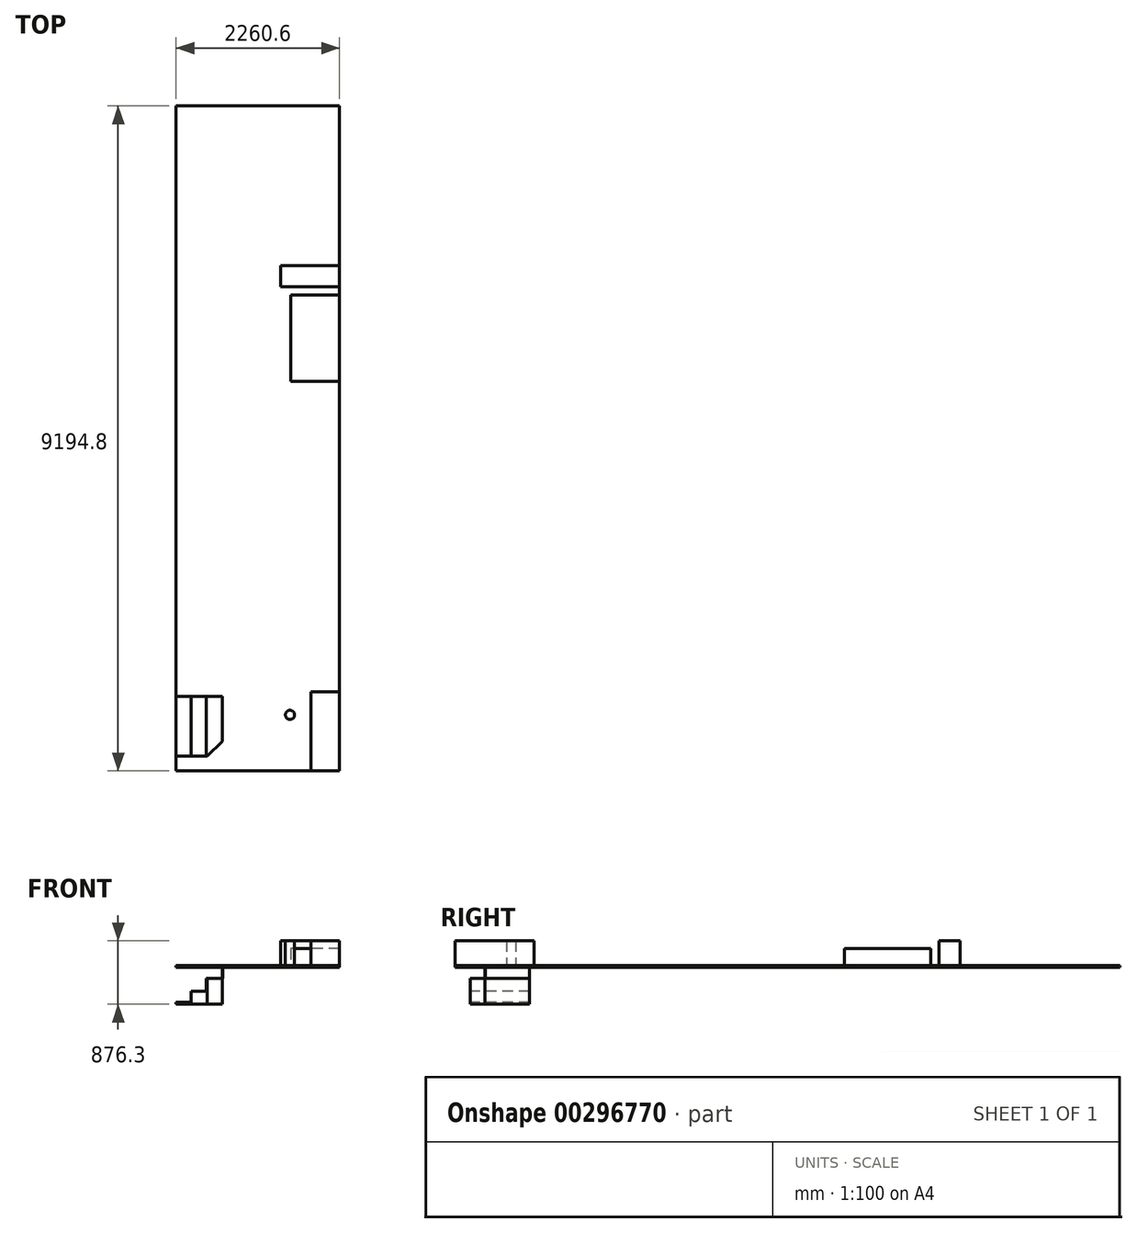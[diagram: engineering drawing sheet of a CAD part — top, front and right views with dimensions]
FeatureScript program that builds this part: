
annotation { "Feature Type Name" : "Feature", "Feature Type Description" : "" }
export const myFeature = defineFeature(function(context is Context, id is Id, definition is map)
    precondition{}
    {
        {
            var Q0;
            Q0=qCreatedBy(makeId("Top.planeOp"),FACE);
            var sketch = newSketch(context, id + "F0", { "sketchPlane" : qUnion([Q0])});
            skLineSegment(sketch, "E0.bottom", {"start": v(0, 0) * mm, "end": v(1016, 0) * mm});
            skLineSegment(sketch, "E0.top", {"start": v(0, 1930.4) * mm, "end": v(1016, 1930.4) * mm});
            skLineSegment(sketch, "E0.left", {"start": v(0, 0) * mm, "end": v(0, 1930.4) * mm});
            skLineSegment(sketch, "E0.right", {"start": v(1016, 0) * mm, "end": v(1016, 1930.4) * mm});
            skLineSegment(sketch, "E1.bottom", {"start": v(1016, 1930.4) * mm, "end": v(-203.2, 1930.4) * mm});
            skLineSegment(sketch, "E1.top", {"start": v(1016, 4064) * mm, "end": v(-203.2, 4064) * mm});
            skLineSegment(sketch, "E1.left", {"start": v(1016, 1930.4) * mm, "end": v(1016, 4064) * mm});
            skLineSegment(sketch, "E1.right", {"start": v(-203.2, 1930.4) * mm, "end": v(-203.2, 4064) * mm});
            skLineSegment(sketch, "E2.bottom", {"start": v(-1244.6, 635) * mm, "end": v(-635, 635) * mm});
            skLineSegment(sketch, "E2.left", {"start": v(-1244.6, 635) * mm, "end": v(-1244.6, 1244.6) * mm});
            skLineSegment(sketch, "E2.right", {"start": v(-635, 635) * mm, "end": v(-635, 1270) * mm});
            skLineSegment(sketch, "E3", {"start": v(-1244.6, 1244.6) * mm, "end": v(-1244.6, 1651) * mm});
            skLineSegment(sketch, "E4", {"start": v(-1244.6, 1651) * mm, "end": v(-635, 1270) * mm});
            skLineSegment(sketch, "E5.bottom", {"start": v(1016, 0) * mm, "end": v(-1244.6, 0) * mm});
            skLineSegment(sketch, "E5.top", {"start": v(1016, 4165.6) * mm, "end": v(-1244.6, 4165.6) * mm});
            skLineSegment(sketch, "E5.left", {"start": v(1016, 0) * mm, "end": v(1016, 4165.6) * mm});
            skLineSegment(sketch, "E5.right", {"start": v(-1244.6, 0) * mm, "end": v(-1244.6, 4165.6) * mm});
            skLineSegment(sketch, "E6.top", {"start": v(1016, 5359.4) * mm, "end": v(-1244.6, 5359.4) * mm});
            skLineSegment(sketch, "E6.left", {"start": v(1016, 4165.6) * mm, "end": v(1016, 5359.4) * mm});
            skLineSegment(sketch, "E6.right", {"start": v(-1244.6, 4165.6) * mm, "end": v(-1244.6, 5359.4) * mm});
            skLineSegment(sketch, "E7.top", {"start": v(1016, 7975.6) * mm, "end": v(-1244.6, 7975.6) * mm});
            skLineSegment(sketch, "E7.left", {"start": v(1016, 5359.4) * mm, "end": v(1016, 7975.6) * mm});
            skLineSegment(sketch, "E7.right", {"start": v(-1244.6, 5359.4) * mm, "end": v(-1244.6, 7975.6) * mm});
            skLineSegment(sketch, "E8.bottom", {"start": v(-1244.6, 4165.6) * mm, "end": v(-571.5, 4165.6) * mm});
            skLineSegment(sketch, "E8.top", {"start": v(-1244.6, 5359.4) * mm, "end": v(-571.5, 5359.4) * mm});
            skLineSegment(sketch, "E8.right", {"start": v(-571.5, 4165.6) * mm, "end": v(-571.5, 5359.4) * mm});
            skLineSegment(sketch, "E9", {"start": v(-114.3, 5359.4) * mm, "end": v(-114.3, 4165.6) * mm, "construction": true});
            skLineSegment(sketch, "E10.MirrorCS", {"start": v(342.9, 4165.6) * mm, "end": v(342.9, 5359.4) * mm});
            skLineSegment(sketch, "E11.MirrorCS", {"start": v(1016, 4165.6) * mm, "end": v(342.9, 4165.6) * mm});
            skLineSegment(sketch, "E12.MirrorCS", {"start": v(1016, 5359.4) * mm, "end": v(342.9, 5359.4) * mm});
            skLineSegment(sketch, "E13.bottom", {"start": v(-609.6, 7975.6) * mm, "end": v(381, 7975.6) * mm});
            skLineSegment(sketch, "E13.top", {"start": v(-609.6, 8026.4) * mm, "end": v(381, 8026.4) * mm});
            skLineSegment(sketch, "E13.left", {"start": v(-609.6, 7975.6) * mm, "end": v(-609.6, 8026.4) * mm});
            skLineSegment(sketch, "E13.right", {"start": v(381, 7975.6) * mm, "end": v(381, 8026.4) * mm});
            skLineSegment(sketch, "E14.bottom", {"start": v(-1244.6, 0) * mm, "end": v(1016, 0) * mm});
            skLineSegment(sketch, "E14.top", {"start": v(-1244.6, -1219.2) * mm, "end": v(1016, -1219.2) * mm});
            skLineSegment(sketch, "E14.left", {"start": v(-1244.6, 0) * mm, "end": v(-1244.6, -1219.2) * mm});
            skLineSegment(sketch, "E14.right", {"start": v(1016, 0) * mm, "end": v(1016, -1219.2) * mm});
            skLineSegment(sketch, "E15", {"start": v(-1244.6, 0) * mm, "end": v(-1244.6, -190.5) * mm});
            skLineSegment(sketch, "E16", {"start": v(-1244.6, -190.5) * mm, "end": v(-596.9, -190.5) * mm});
            skLineSegment(sketch, "E17", {"start": v(-596.9, -190.5) * mm, "end": v(-596.9, -800.1) * mm});
            skLineSegment(sketch, "E18", {"start": v(-596.9, -800.1) * mm, "end": v(-812.43, -1015.63) * mm});
            skLineSegment(sketch, "E19", {"start": v(-812.43, -1015.63) * mm, "end": v(-1244.6, -1015.63) * mm});
            skLineSegment(sketch, "E20", {"start": v(-826.95, -190.5) * mm, "end": v(-826.95, -1015.63) * mm});
            skLineSegment(sketch, "E21", {"start": v(-1035.43, -190.5) * mm, "end": v(-1035.43, -1015.63) * mm});
            skLineSegment(sketch, "E22", {"start": v(-609.16, -190.5) * mm, "end": v(-609.16, -812.36) * mm});
            skSolve(sketch);
        }
        {
            var Q0;
            {var subQ2=sQuery(id+"F0.wireOp",EDGE,"E0.left");Q0=makeQuery(id+"F0.imprint","IMPRINT",FACE,{"disambiguationData":[TD([[makeQuery(id+"F0.imprint","IMPRINT",EDGE,{"derivedFrom":subQ2}),1.0]])]});}
            var Q1;
            {var subQ1=sQuery(id+"F0.wireOp",EDGE,"E1.top");Q1=makeQuery(id+"F0.imprint","IMPRINT",FACE,{"disambiguationData":[TD([[makeQuery(id+"F0.imprint","IMPRINT",EDGE,{"derivedFrom":subQ1}),1.0]])]});}
            var Q2;
            {var subQ0=sQuery(id+"F0.wireOp",EDGE,"E0.left");Q2=makeQuery(id+"F0.imprint","IMPRINT",FACE,{"disambiguationData":[TD([[makeQuery(id+"F0.imprint","IMPRINT",EDGE,{"derivedFrom":subQ0}),-1.0]])]});}
            var Q3;
            {var subQ0=sQuery(id+"F0.wireOp",EDGE,"E2.bottom");Q3=makeQuery(id+"F0.imprint","IMPRINT",FACE,{"disambiguationData":[TD([[makeQuery(id+"F0.imprint","IMPRINT",EDGE,{"derivedFrom":subQ0}),1.0]])]});}
            var Q4;
            Q4=makeQuery(id+"F0.imprint","IMPRINT",FACE,{"disambiguationData":[TD([[makeQuery(id+"F0.imprint","IMPRINT",EDGE,{"derivedFrom":sQuery(id+"F0.wireOp",EDGE,"E5.top")}),-1.0]])]});
            var Q5;
            Q5=makeQuery(id+"F0.imprint","IMPRINT",FACE,{"disambiguationData":[TD([[makeQuery(id+"F0.imprint","IMPRINT",EDGE,{"derivedFrom":sQuery(id+"F0.wireOp",EDGE,"E6.top")}),-1.0]])]});
            var Q6;
            Q6=makeQuery(id+"F0.imprint","IMPRINT",FACE,{"disambiguationData":[TD([[makeQuery(id+"F0.imprint","IMPRINT",EDGE,{"derivedFrom":sQuery(id+"F0.wireOp",EDGE,"E13.bottom")}),1.0]])]});
            var Q7;
            {var subQ11=sQuery(id+"F0.wireOp",EDGE,"E14.top");Q7=makeQuery(id+"F0.imprint","IMPRINT",FACE,{"disambiguationData":[TD([[makeQuery(id+"F0.imprint","IMPRINT",EDGE,{"derivedFrom":subQ11}),1.0]])]});}
            extrude(context, id + "F1", {"entities" : qUnion([Q0, Q1, Q2, Q3, Q4, Q5, Q6, Q7]), "oppositeDirection" : true, "depth" : 25.4 * mm, "offsetDistance" : 25.4 * mm});
        }
        {
            var Q0;
            Q0=makeQuery(id+"F0.imprint","IMPRINT",FACE,{"disambiguationData":[TD([[makeQuery(id+"F0.imprint","IMPRINT",EDGE,{"derivedFrom":sQuery(id+"F0.wireOp",EDGE,"E8.bottom")}),1.0]])]});
            var Q1;
            Q1=makeQuery(id+"F0.imprint","IMPRINT",FACE,{"disambiguationData":[TD([[makeQuery(id+"F0.imprint","IMPRINT",EDGE,{"derivedFrom":sQuery(id+"F0.wireOp",EDGE,"E6.left")}),1.0]])]});
            extrude(context, id + "F2", {"entities" : qUnion([Q0, Q1]), "depth" : 234.95 * mm, "offsetDistance" : 25.4 * mm});
        }
        {
            var Q0;
            {var subQ2=sQuery(id+"F0.wireOp",EDGE,"E0.left");Q0=makeQuery(id+"F0.imprint","IMPRINT",FACE,{"disambiguationData":[TD([[makeQuery(id+"F0.imprint","IMPRINT",EDGE,{"derivedFrom":subQ2}),1.0]])]});}
            var sketch = newSketch(context, id + "F3", { "sketchPlane" : qUnion([Q0])});
            skLineSegment(sketch, "E23.0.0", {"start": v(0, 0) * mm, "end": v(1016, 0) * mm});
            skLineSegment(sketch, "E23.0.1", {"start": v(1016, 0) * mm, "end": v(1016, 1930.4) * mm});
            skLineSegment(sketch, "E23.0.2", {"start": v(1016, 1930.4) * mm, "end": v(0, 1930.4) * mm});
            skLineSegment(sketch, "E23.0.3", {"start": v(0, 1930.4) * mm, "end": v(0, 0) * mm});
            skLineSegment(sketch, "E24.0.0", {"start": v(0, 1930.4) * mm, "end": v(1016, 1930.4) * mm});
            skLineSegment(sketch, "E24.0.1", {"start": v(1016, 1930.4) * mm, "end": v(1016, 4064) * mm});
            skLineSegment(sketch, "E24.0.2", {"start": v(1016, 4064) * mm, "end": v(-203.2, 4064) * mm});
            skLineSegment(sketch, "E24.0.3", {"start": v(-203.2, 4064) * mm, "end": v(-203.2, 1930.4) * mm});
            skLineSegment(sketch, "E24.0.4", {"start": v(-203.2, 1930.4) * mm, "end": v(0, 1930.4) * mm});
            skLineSegment(sketch, "E25.0.0", {"start": v(-1244.6, 1651) * mm, "end": v(-1244.6, 635) * mm});
            skLineSegment(sketch, "E25.0.1", {"start": v(-1244.6, 635) * mm, "end": v(-635, 635) * mm});
            skLineSegment(sketch, "E25.0.2", {"start": v(-635, 635) * mm, "end": v(-635, 1270) * mm});
            skLineSegment(sketch, "E25.0.3", {"start": v(-635, 1270) * mm, "end": v(-1244.6, 1651) * mm});
            skSolve(sketch);
        }
        {
            var Q0;
            {var subQ13=sQuery(id+"F0.wireOp",EDGE,"E14.top");Q0=makeQuery(id+"F0.imprint","IMPRINT",FACE,{"disambiguationData":[TD([[makeQuery(id+"F0.imprint","IMPRINT",EDGE,{"derivedFrom":subQ13}),1.0]])]});}
            var sketch = newSketch(context, id + "F4", { "sketchPlane" : qUnion([Q0])});
            skLineSegment(sketch, "E26.bottom", {"start": v(1016, 5473.7) * mm, "end": v(203.2, 5473.7) * mm});
            skLineSegment(sketch, "E26.top", {"start": v(1016, 5765.8) * mm, "end": v(203.2, 5765.8) * mm});
            skLineSegment(sketch, "E26.left", {"start": v(1016, 5473.7) * mm, "end": v(1016, 5765.8) * mm});
            skLineSegment(sketch, "E26.right", {"start": v(203.2, 5473.7) * mm, "end": v(203.2, 5765.8) * mm});
            skLineSegment(sketch, "E27", {"start": v(-596.9, -444.5) * mm, "end": v(330.2, -444.5) * mm, "construction": true});
            skLineSegment(sketch, "E28", {"start": v(330.2, -444.5) * mm, "end": v(330.2, 0) * mm, "construction": true});
            skCircle(sketch, "E29", {"center": v(330.2, -444.5) * mm, "radius": 63.5 * mm});
            skLineSegment(sketch, "E30.bottom", {"start": v(622.3, -127) * mm, "end": v(1016, -127) * mm});
            skLineSegment(sketch, "E30.top", {"start": v(622.3, -1219.2) * mm, "end": v(1016, -1219.2) * mm});
            skLineSegment(sketch, "E30.left", {"start": v(622.3, -127) * mm, "end": v(622.3, -1219.2) * mm});
            skLineSegment(sketch, "E30.right", {"start": v(1016, -127) * mm, "end": v(1016, -1219.2) * mm});
            skSolve(sketch);
        }
        {
            var Q0;
            Q0 = qSketchRegion(id + "F4", true);
            extrude(context, id + "F5", {"entities" : qUnion([Q0]), "depth" : 342.9 * mm, "offsetDistance" : 25.4 * mm});
        }
        {
            var Q0;
            {var subQ3=sQuery(id+"F0.wireOp",EDGE,"E17");Q0=makeQuery(id+"F0.imprint","IMPRINT",FACE,{"disambiguationData":[TD([[makeQuery(id+"F0.imprint","IMPRINT",EDGE,{"derivedFrom":subQ3}),-1.0]])]});}
            extrude(context, id + "F6", {"entities" : qUnion([Q0]), "oppositeDirection" : true, "depth" : 177.8 * mm, "offsetDistance" : 25.4 * mm});
        }
        {
            var Q0;
            {var subQ5=sQuery(id+"F0.wireOp",EDGE,"E21");Q0=makeQuery(id+"F0.imprint","IMPRINT",FACE,{"disambiguationData":[TD([[makeQuery(id+"F0.imprint","IMPRINT",EDGE,{"derivedFrom":subQ5}),-1.0]])]});}
            var Q1;
            {var subQ0=sQuery(id+"F0.wireOp",EDGE,"E20");Q1=makeQuery(id+"F0.imprint","IMPRINT",FACE,{"disambiguationData":[TD([[makeQuery(id+"F0.imprint","IMPRINT",EDGE,{"derivedFrom":subQ0}),-1.0]])]});}
            var Q2;
            {var subQ0=sQuery(id+"F0.wireOp",EDGE,"E20");Q2=makeQuery(id+"F0.imprint","IMPRINT",FACE,{"disambiguationData":[TD([[makeQuery(id+"F0.imprint","IMPRINT",EDGE,{"derivedFrom":subQ0}),1.0]])]});}
            extrude(context, id + "F7", {"entities" : qUnion([Q0, Q1, Q2]), "operationType" : NewBodyOperationType.ADD, "oppositeDirection" : true, "depth" : 533.4 * mm, "offsetDistance" : 25.4 * mm});
        }
        {
            var Q0;
            {var subQ5=sQuery(id+"F0.wireOp",EDGE,"E21");Q0=makeQuery(id+"F0.imprint","IMPRINT",FACE,{"disambiguationData":[TD([[makeQuery(id+"F0.imprint","IMPRINT",EDGE,{"derivedFrom":subQ5}),-1.0]])]});}
            extrude(context, id + "F8", {"entities" : qUnion([Q0]), "operationType" : NewBodyOperationType.REMOVE, "oppositeDirection" : true, "depth" : 508 * mm, "offsetDistance" : 25.4 * mm});
        }
        {
            var Q0;
            {var subQ0=sQuery(id+"F0.wireOp",EDGE,"E20");Q0=makeQuery(id+"F0.imprint","IMPRINT",FACE,{"disambiguationData":[TD([[makeQuery(id+"F0.imprint","IMPRINT",EDGE,{"derivedFrom":subQ0}),-1.0]])]});}
            extrude(context, id + "F9", {"entities" : qUnion([Q0]), "operationType" : NewBodyOperationType.REMOVE, "oppositeDirection" : true, "depth" : 355.6 * mm, "offsetDistance" : 25.4 * mm});
        }
        {
            var Q0;
            {var subQ0=sQuery(id+"F0.wireOp",EDGE,"E20");Q0=makeQuery(id+"F0.imprint","IMPRINT",FACE,{"disambiguationData":[TD([[makeQuery(id+"F0.imprint","IMPRINT",EDGE,{"derivedFrom":subQ0}),1.0]])]});}
            extrude(context, id + "F10", {"entities" : qUnion([Q0]), "operationType" : NewBodyOperationType.REMOVE, "oppositeDirection" : true, "depth" : 177.8 * mm, "offsetDistance" : 25.4 * mm});
        }
    });
